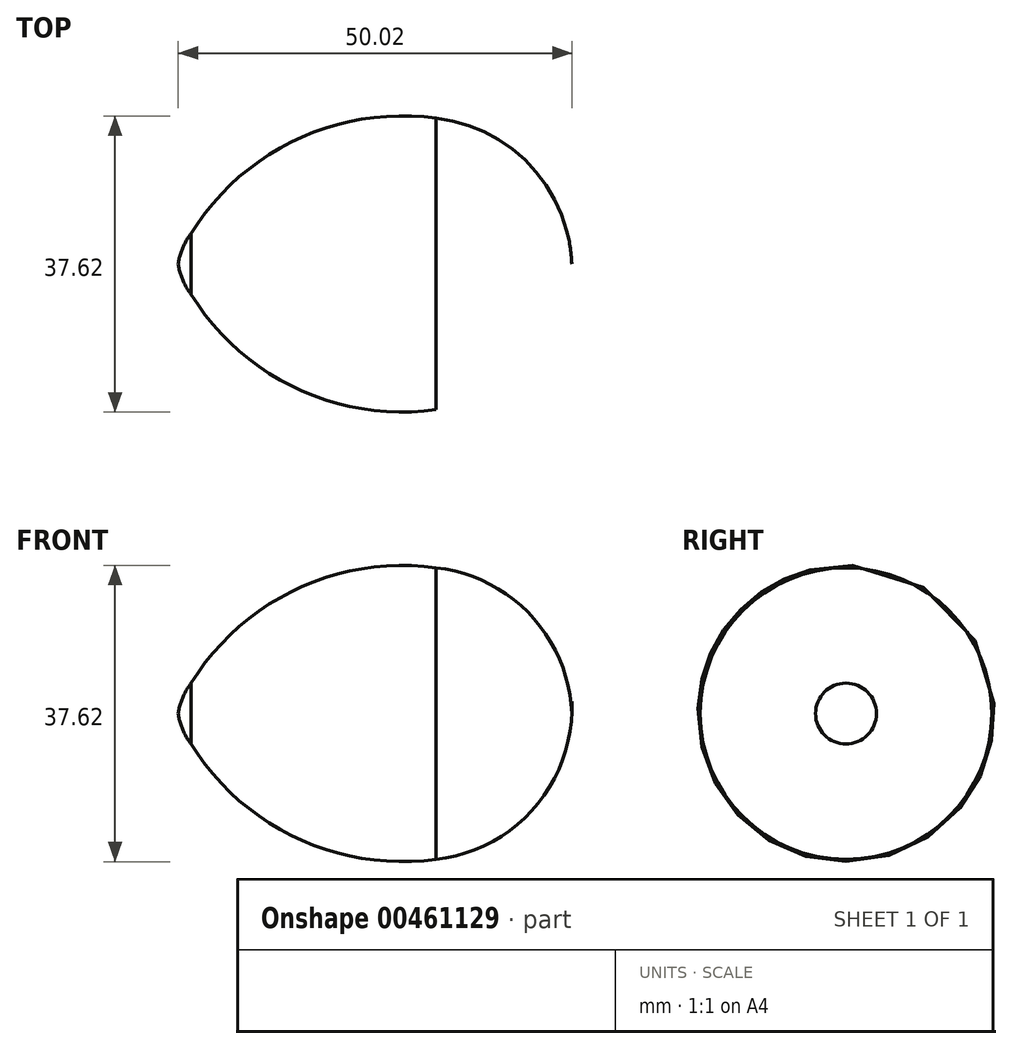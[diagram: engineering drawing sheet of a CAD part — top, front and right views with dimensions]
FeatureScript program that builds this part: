
annotation { "Feature Type Name" : "Feature", "Feature Type Description" : "" }
export const myFeature = defineFeature(function(context is Context, id is Id, definition is map)
    precondition{}
    {
        {
            var Q0;
            Q0=qCreatedBy(makeId("Front.planeOp"),FACE);
            var sketch = newSketch(context, id + "F0", { "sketchPlane" : qUnion([Q0])});
            skLineSegment(sketch, "E0", {"start": v(-28.11, -78.84) * mm, "end": v(-28.11, -71.84) * mm, "construction": true});
            skLineSegment(sketch, "E1", {"start": v(-81.34, -27.34) * mm, "end": v(-31.34, -27.34) * mm});
            skPoint(sketch, "E2.orphan", {"position": v(-94.57, -27.34) * mm});
            skPoint(sketch, "E3.center.orphan", {"position": v(-28.11, -27.34) * mm});
            skPoint(sketch, "E4", {"position": v(46.66, -44.83) * mm});
            skPoint(sketch, "E5", {"position": v(-56.34, -27.34) * mm});
            skLineSegment(sketch, "E6", {"start": v(-48.56, -27.34) * mm, "end": v(-48.56, -8.83) * mm, "construction": true});
            skLineSegment(sketch, "E7", {"start": v(-79.7, -27.34) * mm, "end": v(-79.7, -23.48) * mm, "construction": true});
            skArc(sketch, "E8", {"start": v(-31.34, -27.34) * mm, "mid": v(-36.52, -14.9) * mm, "end": v(-48.56, -8.83) * mm});
            skArc(sketch, "E9", {"start": v(-48.56, -8.83) * mm, "mid": v(-66.3, -11.53) * mm, "end": v(-79.7, -23.48) * mm});
            skArc(sketch, "E10", {"start": v(-79.7, -23.48) * mm, "mid": v(-80.76, -25.3) * mm, "end": v(-81.34, -27.34) * mm});
            skSolve(sketch);
        }
        {
            var Q0;
            Q0 = qSketchRegion(id + "F0", true);
            var Q1;
            Q1=sQuery(id+"F0.wireOp",EDGE,"E1");
            revolve(context, id + "F1", {"entities" : qUnion([Q0]), "axis" : qUnion([Q1]), "revolveType" : RevolveType.FULL});
        }
    });
